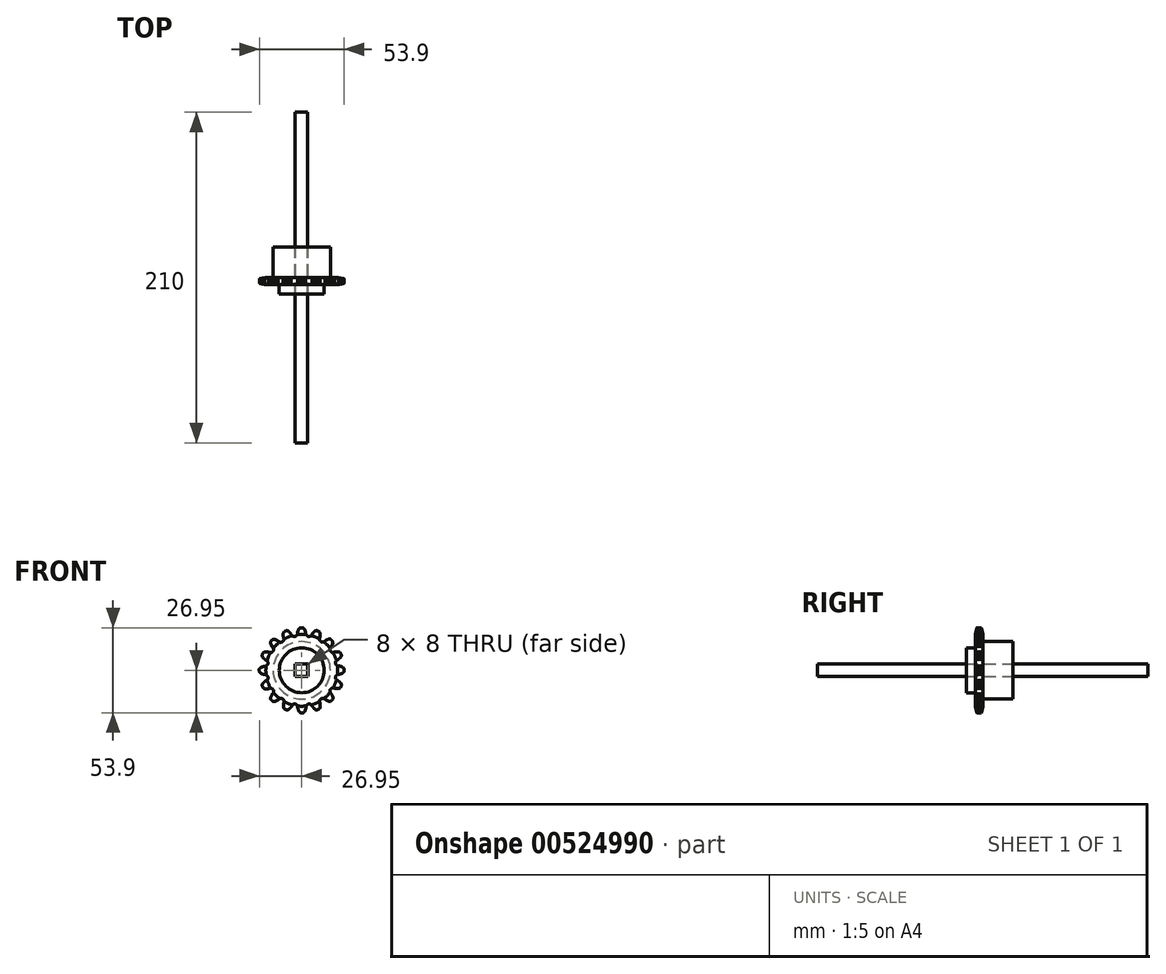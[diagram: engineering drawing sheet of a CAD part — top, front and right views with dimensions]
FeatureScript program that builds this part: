
annotation { "Feature Type Name" : "Feature", "Feature Type Description" : "" }
export const myFeature = defineFeature(function(context is Context, id is Id, definition is map)
    precondition{}
    {
        {
            var Q0;
            Q0=qCreatedBy(makeId("Front.planeOp"),FACE);
            var sketch = newSketch(context, id + "F0", { "sketchPlane" : qUnion([Q0])});
            skCircle(sketch, "E0", {"center": v(0, 0) * mm, "radius": 14.28 * mm});
            skCircle(sketch, "E1", {"center": v(0, 0) * mm, "radius": 26.95 * mm});
            skCircle(sketch, "E2", {"center": v(0, 0) * mm, "radius": 21.9 * mm, "construction": true});
            skArc(sketch, "E3", {"start": v(2.57, 23.85) * mm, "mid": v(4.2, 21.5) * mm, "end": v(6.58, 23.12) * mm});
            skLineSegment(sketch, "E4", {"start": v(2.57, 23.85) * mm, "end": v(1.78, 26.12) * mm});
            skLineSegment(sketch, "E5", {"start": v(1.78, 26.12) * mm, "end": v(0.9, 26.93) * mm});
            skLineSegment(sketch, "E6", {"start": v(6.58, 23.12) * mm, "end": v(8.2, 24.88) * mm});
            skLineSegment(sketch, "E7", {"start": v(8.2, 24.88) * mm, "end": v(9.34, 25.28) * mm});
            skLineSegment(sketch, "E8.1.0", {"start": v(-8.35, 24.81) * mm, "end": v(-9.48, 25.23) * mm});
            skLineSegment(sketch, "E8.1.1", {"start": v(-6.75, 23.02) * mm, "end": v(-8.35, 24.81) * mm});
            skArc(sketch, "E8.1.2", {"start": v(-6.75, 23.02) * mm, "mid": v(-4.34, 21.47) * mm, "end": v(-2.77, 23.88) * mm});
            skLineSegment(sketch, "E8.1.3", {"start": v(-2.77, 23.88) * mm, "end": v(-1.94, 26.13) * mm});
            skLineSegment(sketch, "E8.1.4", {"start": v(-1.94, 26.13) * mm, "end": v(-1.05, 26.93) * mm});
            skLineSegment(sketch, "E8.2.0", {"start": v(-17.21, 19.73) * mm, "end": v(-18.4, 19.68) * mm});
            skLineSegment(sketch, "E8.2.1", {"start": v(-15.05, 18.68) * mm, "end": v(-17.21, 19.73) * mm});
            skArc(sketch, "E8.2.2", {"start": v(-15.05, 18.68) * mm, "mid": v(-12.22, 18.17) * mm, "end": v(-11.7, 21) * mm});
            skLineSegment(sketch, "E8.2.3", {"start": v(-11.7, 21) * mm, "end": v(-11.8, 23.4) * mm});
            skLineSegment(sketch, "E8.2.4", {"start": v(-11.8, 23.4) * mm, "end": v(-11.27, 24.48) * mm});
            skLineSegment(sketch, "E9.2.3.0", {"start": v(-23.45, 11.64) * mm, "end": v(-24.54, 11.14) * mm});
            skLineSegment(sketch, "E9.3.3.0", {"start": v(-21.05, 11.5) * mm, "end": v(-23.45, 11.64) * mm});
            skArc(sketch, "E9.6.3.0", {"start": v(-21.05, 11.5) * mm, "mid": v(-18.24, 12.11) * mm, "end": v(-18.84, 14.93) * mm});
            skLineSegment(sketch, "E9.10.3.0", {"start": v(-18.84, 14.93) * mm, "end": v(-19.85, 17.1) * mm});
            skLineSegment(sketch, "E9.13.3.0", {"start": v(-19.85, 17.1) * mm, "end": v(-19.78, 18.3) * mm});
            skLineSegment(sketch, "E9.2.4.0", {"start": v(-26.12, 1.78) * mm, "end": v(-26.93, 0.9) * mm});
            skLineSegment(sketch, "E9.3.4.0", {"start": v(-23.85, 2.57) * mm, "end": v(-26.12, 1.78) * mm});
            skArc(sketch, "E9.6.4.0", {"start": v(-23.85, 2.57) * mm, "mid": v(-21.5, 4.2) * mm, "end": v(-23.12, 6.58) * mm});
            skLineSegment(sketch, "E9.10.4.0", {"start": v(-23.12, 6.58) * mm, "end": v(-24.88, 8.2) * mm});
            skLineSegment(sketch, "E9.13.4.0", {"start": v(-24.88, 8.2) * mm, "end": v(-25.28, 9.34) * mm});
            skLineSegment(sketch, "E9.2.5.0", {"start": v(-24.81, -8.35) * mm, "end": v(-25.23, -9.48) * mm});
            skLineSegment(sketch, "E9.3.5.0", {"start": v(-23.02, -6.75) * mm, "end": v(-24.81, -8.35) * mm});
            skArc(sketch, "E9.6.5.0", {"start": v(-23.02, -6.75) * mm, "mid": v(-21.47, -4.34) * mm, "end": v(-23.88, -2.77) * mm});
            skLineSegment(sketch, "E9.10.5.0", {"start": v(-23.88, -2.77) * mm, "end": v(-26.13, -1.94) * mm});
            skLineSegment(sketch, "E9.13.5.0", {"start": v(-26.13, -1.94) * mm, "end": v(-26.93, -1.05) * mm});
            skLineSegment(sketch, "E9.2.6.0", {"start": v(-19.73, -17.21) * mm, "end": v(-19.68, -18.4) * mm});
            skLineSegment(sketch, "E9.3.6.0", {"start": v(-18.68, -15.05) * mm, "end": v(-19.73, -17.21) * mm});
            skArc(sketch, "E9.6.6.0", {"start": v(-18.68, -15.05) * mm, "mid": v(-18.17, -12.22) * mm, "end": v(-21, -11.7) * mm});
            skLineSegment(sketch, "E9.10.6.0", {"start": v(-21, -11.7) * mm, "end": v(-23.4, -11.8) * mm});
            skLineSegment(sketch, "E9.13.6.0", {"start": v(-23.4, -11.8) * mm, "end": v(-24.48, -11.27) * mm});
            skLineSegment(sketch, "E9.2.7.0", {"start": v(-11.64, -23.45) * mm, "end": v(-11.14, -24.54) * mm});
            skLineSegment(sketch, "E9.3.7.0", {"start": v(-11.5, -21.05) * mm, "end": v(-11.64, -23.45) * mm});
            skArc(sketch, "E9.6.7.0", {"start": v(-11.5, -21.05) * mm, "mid": v(-12.11, -18.24) * mm, "end": v(-14.93, -18.84) * mm});
            skLineSegment(sketch, "E9.10.7.0", {"start": v(-14.93, -18.84) * mm, "end": v(-17.1, -19.85) * mm});
            skLineSegment(sketch, "E9.13.7.0", {"start": v(-17.1, -19.85) * mm, "end": v(-18.3, -19.78) * mm});
            skLineSegment(sketch, "E9.2.8.0", {"start": v(-1.78, -26.12) * mm, "end": v(-0.9, -26.93) * mm});
            skLineSegment(sketch, "E9.3.8.0", {"start": v(-2.57, -23.85) * mm, "end": v(-1.78, -26.12) * mm});
            skArc(sketch, "E9.6.8.0", {"start": v(-2.57, -23.85) * mm, "mid": v(-4.2, -21.5) * mm, "end": v(-6.58, -23.12) * mm});
            skLineSegment(sketch, "E9.10.8.0", {"start": v(-6.58, -23.12) * mm, "end": v(-8.2, -24.88) * mm});
            skLineSegment(sketch, "E9.13.8.0", {"start": v(-8.2, -24.88) * mm, "end": v(-9.34, -25.28) * mm});
            skLineSegment(sketch, "E9.2.9.0", {"start": v(8.35, -24.81) * mm, "end": v(9.48, -25.23) * mm});
            skLineSegment(sketch, "E9.3.9.0", {"start": v(6.75, -23.02) * mm, "end": v(8.35, -24.81) * mm});
            skArc(sketch, "E9.6.9.0", {"start": v(6.75, -23.02) * mm, "mid": v(4.34, -21.47) * mm, "end": v(2.77, -23.88) * mm});
            skLineSegment(sketch, "E9.10.9.0", {"start": v(2.77, -23.88) * mm, "end": v(1.94, -26.13) * mm});
            skLineSegment(sketch, "E9.13.9.0", {"start": v(1.94, -26.13) * mm, "end": v(1.05, -26.93) * mm});
            skLineSegment(sketch, "E9.2.10.0", {"start": v(17.21, -19.73) * mm, "end": v(18.4, -19.68) * mm});
            skLineSegment(sketch, "E9.3.10.0", {"start": v(15.05, -18.68) * mm, "end": v(17.21, -19.73) * mm});
            skArc(sketch, "E9.6.10.0", {"start": v(15.05, -18.68) * mm, "mid": v(12.22, -18.17) * mm, "end": v(11.7, -21) * mm});
            skLineSegment(sketch, "E9.10.10.0", {"start": v(11.7, -21) * mm, "end": v(11.8, -23.4) * mm});
            skLineSegment(sketch, "E9.13.10.0", {"start": v(11.8, -23.4) * mm, "end": v(11.27, -24.48) * mm});
            skLineSegment(sketch, "E9.2.11.0", {"start": v(23.45, -11.64) * mm, "end": v(24.54, -11.14) * mm});
            skLineSegment(sketch, "E9.3.11.0", {"start": v(21.05, -11.5) * mm, "end": v(23.45, -11.64) * mm});
            skArc(sketch, "E9.6.11.0", {"start": v(21.05, -11.5) * mm, "mid": v(18.24, -12.11) * mm, "end": v(18.84, -14.93) * mm});
            skLineSegment(sketch, "E9.10.11.0", {"start": v(18.84, -14.93) * mm, "end": v(19.85, -17.1) * mm});
            skLineSegment(sketch, "E9.13.11.0", {"start": v(19.85, -17.1) * mm, "end": v(19.78, -18.3) * mm});
            skLineSegment(sketch, "E9.2.12.0", {"start": v(26.12, -1.78) * mm, "end": v(26.93, -0.9) * mm});
            skLineSegment(sketch, "E9.3.12.0", {"start": v(23.85, -2.57) * mm, "end": v(26.12, -1.78) * mm});
            skArc(sketch, "E9.6.12.0", {"start": v(23.85, -2.57) * mm, "mid": v(21.5, -4.2) * mm, "end": v(23.12, -6.58) * mm});
            skLineSegment(sketch, "E9.10.12.0", {"start": v(23.12, -6.58) * mm, "end": v(24.88, -8.2) * mm});
            skLineSegment(sketch, "E9.13.12.0", {"start": v(24.88, -8.2) * mm, "end": v(25.28, -9.34) * mm});
            skLineSegment(sketch, "E9.2.13.0", {"start": v(24.81, 8.35) * mm, "end": v(25.23, 9.48) * mm});
            skLineSegment(sketch, "E9.3.13.0", {"start": v(23.02, 6.75) * mm, "end": v(24.81, 8.35) * mm});
            skArc(sketch, "E9.6.13.0", {"start": v(23.02, 6.75) * mm, "mid": v(21.47, 4.34) * mm, "end": v(23.88, 2.77) * mm});
            skLineSegment(sketch, "E9.10.13.0", {"start": v(23.88, 2.77) * mm, "end": v(26.13, 1.94) * mm});
            skLineSegment(sketch, "E9.13.13.0", {"start": v(26.13, 1.94) * mm, "end": v(26.93, 1.05) * mm});
            skLineSegment(sketch, "E9.2.14.0", {"start": v(19.73, 17.21) * mm, "end": v(19.68, 18.4) * mm});
            skLineSegment(sketch, "E9.3.14.0", {"start": v(18.68, 15.05) * mm, "end": v(19.73, 17.21) * mm});
            skArc(sketch, "E9.6.14.0", {"start": v(18.68, 15.05) * mm, "mid": v(18.17, 12.22) * mm, "end": v(21, 11.7) * mm});
            skLineSegment(sketch, "E9.10.14.0", {"start": v(21, 11.7) * mm, "end": v(23.4, 11.8) * mm});
            skLineSegment(sketch, "E9.13.14.0", {"start": v(23.4, 11.8) * mm, "end": v(24.48, 11.27) * mm});
            skLineSegment(sketch, "E9.2.15.0", {"start": v(11.64, 23.45) * mm, "end": v(11.14, 24.54) * mm});
            skLineSegment(sketch, "E9.3.15.0", {"start": v(11.5, 21.05) * mm, "end": v(11.64, 23.45) * mm});
            skArc(sketch, "E9.6.15.0", {"start": v(11.5, 21.05) * mm, "mid": v(12.11, 18.24) * mm, "end": v(14.93, 18.84) * mm});
            skLineSegment(sketch, "E9.10.15.0", {"start": v(14.93, 18.84) * mm, "end": v(17.1, 19.85) * mm});
            skLineSegment(sketch, "E9.13.15.0", {"start": v(17.1, 19.85) * mm, "end": v(18.3, 19.78) * mm});
            skSolve(sketch);
        }
        {
            var Q0;
            Q0=makeQuery(id+"F0.imprint","IMPRINT",FACE,{"disambiguationData":[TD([[makeQuery(id+"F0.imprint","IMPRINT",EDGE,{"derivedFrom":sQuery(id+"F0.wireOp",EDGE,"E0")}),-1.0]])]});
            extrude(context, id + "F1", {"entities" : qUnion([Q0]), "depth" : 4.5 * mm, "offsetDistance" : 25 * mm});
        }
        {
            var Q0;
            Q0=qCreatedBy(makeId("Right.planeOp"),FACE);
            var sketch = newSketch(context, id + "F2", { "sketchPlane" : qUnion([Q0])});
            skLineSegment(sketch, "E10.bottom", {"start": v(-7.87, 18.82) * mm, "end": v(-5.25, 18.82) * mm});
            skLineSegment(sketch, "E10.top", {"start": v(-7.87, 36.62) * mm, "end": v(3.37, 36.62) * mm});
            skLineSegment(sketch, "E10.left", {"start": v(-7.87, 18.82) * mm, "end": v(-7.87, 36.62) * mm});
            skLineSegment(sketch, "E10.right", {"start": v(3.37, 18.82) * mm, "end": v(3.37, 36.62) * mm});
            skPoint(sketch, "E11", {"position": v(-2.25, 18.82) * mm});
            skLineSegment(sketch, "E12", {"start": v(-5.25, 18.82) * mm, "end": v(-2.25, 34.82) * mm});
            skLineSegment(sketch, "E13", {"start": v(-2.25, 34.82) * mm, "end": v(0.75, 18.82) * mm});
            skLineSegment(sketch, "E14.trimOffspring", {"start": v(0.75, 18.82) * mm, "end": v(3.37, 18.82) * mm});
            skSolve(sketch);
        }
        {
            var Q0;
            Q0=makeQuery(id+"F2.imprint","IMPRINT",FACE,{"disambiguationData":[TD([[makeQuery(id+"F2.imprint","IMPRINT",EDGE,{"derivedFrom":sQuery(id+"F2.wireOp",EDGE,"E10.bottom")}),1.0]])]});
            var Q1;
            Q1=makeQuery(id+"F1.opExtrude","SWEPT_FACE",FACE,{"disambiguationData":[OSD([sQuery(id+"F0.wireOp",EDGE,"E0")])]});
            revolve(context, id + "F3", {"operationType" : NewBodyOperationType.REMOVE, "entities" : qUnion([Q0]), "axis" : qUnion([Q1]), "revolveType" : RevolveType.FULL, "oppositeDirection" : true});
        }
        {
            var Q0;
            Q0=qCreatedBy(makeId("Front.planeOp"),FACE);
            var sketch = newSketch(context, id + "F4", { "sketchPlane" : qUnion([Q0])});
            skCircle(sketch, "E15", {"center": v(0, 0) * mm, "radius": 14.28 * mm});
            skCircle(sketch, "E16", {"center": v(0, 0) * mm, "radius": 18.2 * mm});
            skSolve(sketch);
        }
        {
            var Q0;
            Q0 = qSketchRegion(id + "F4", true);
            var Q1;
            Q1=makeQuery(id+"F4.imprint","IMPRINT",FACE,{"disambiguationData":[TD([[makeQuery(id+"F4.imprint","IMPRINT",EDGE,{"derivedFrom":sQuery(id+"F4.wireOp",EDGE,"E15")}),-1.0]])]});
            var Q2;
            Q2=makeQuery(id+"F4.imprint","IMPRINT",FACE,{"disambiguationData":[TD([[makeQuery(id+"F4.imprint","IMPRINT",EDGE,{"derivedFrom":sQuery(id+"F4.wireOp",EDGE,"E15")}),1.0]])]});
            extrude(context, id + "F5", {"entities" : qUnion([Q0, Q1, Q2]), "operationType" : NewBodyOperationType.ADD, "oppositeDirection" : true, "depth" : 19.3 * mm, "offsetDistance" : 25 * mm});
        }
        {
            var Q0;
            Q0=makeQuery(id+"F4.imprint","IMPRINT",FACE,{"disambiguationData":[TD([[makeQuery(id+"F4.imprint","IMPRINT",EDGE,{"derivedFrom":sQuery(id+"F4.wireOp",EDGE,"E15")}),1.0]])]});
            extrude(context, id + "F6", {"entities" : qUnion([Q0]), "operationType" : NewBodyOperationType.ADD, "depth" : 10.5 * mm, "offsetDistance" : 25 * mm});
        }
        {
            var Q0;
            Q0=makeQuery(id+"F5.opExtrude","CAP_FACE",FACE,{"disambiguationData":[OSD([sQuery(id+"F4.wireOp",EDGE,"E16")])],"isStart":false});
            var sketch = newSketch(context, id + "F7", { "sketchPlane" : qUnion([Q0])});
            skCircle(sketch, "E17.cCircle", {"center": v(0, 0) * mm, "radius": 5.66 * mm, "construction": true});
            skLineSegment(sketch, "E17.0", {"start": v(-4, 4) * mm, "end": v(4, 4) * mm});
            skLineSegment(sketch, "E17.1", {"start": v(4, 4) * mm, "end": v(4, -4) * mm});
            skLineSegment(sketch, "E17.2", {"start": v(4, -4) * mm, "end": v(-4, -4) * mm});
            skLineSegment(sketch, "E17.3", {"start": v(-4, -4) * mm, "end": v(-4, 4) * mm});
            skSolve(sketch);
        }
        {
            var Q0;
            Q0 = qSketchRegion(id + "F7", true);
            var Q1;
            Q1=makeQuery(id+"F7.imprint","IMPRINT",FACE,{"disambiguationData":[TD([[makeQuery(id+"F7.imprint","IMPRINT",EDGE,{"derivedFrom":sQuery(id+"F7.wireOp",EDGE,"E17.0")}),-1.0]])]});
            extrude(context, id + "F8", {"entities" : qUnion([Q0, Q1]), "operationType" : NewBodyOperationType.REMOVE, "endBound" : BoundingType.THROUGH_ALL, "oppositeDirection" : true, "depth" : 25 * mm, "offsetDistance" : 25 * mm});
        }
        {
            var Q0;
            Q0=qCreatedBy(makeId("Front.planeOp"),FACE);
            var sketch = newSketch(context, id + "F9", { "sketchPlane" : qUnion([Q0])});
            skLineSegment(sketch, "E18.bottom", {"start": v(-4.11, 3.95) * mm, "end": v(3.79, 3.95) * mm});
            skLineSegment(sketch, "E18.top", {"start": v(-4.11, -3.95) * mm, "end": v(3.79, -3.95) * mm});
            skLineSegment(sketch, "E18.left", {"start": v(-4.11, 3.95) * mm, "end": v(-4.11, -3.95) * mm});
            skLineSegment(sketch, "E18.right", {"start": v(3.79, 3.95) * mm, "end": v(3.79, -3.95) * mm});
            skSolve(sketch);
        }
        {
            var Q0;
            Q0 = qSketchRegion(id + "F9", true);
            var Q1;
            Q1=makeQuery(id+"F9.imprint","IMPRINT",FACE,{"disambiguationData":[TD([[makeQuery(id+"F9.imprint","IMPRINT",EDGE,{"derivedFrom":sQuery(id+"F9.wireOp",EDGE,"E18.bottom")}),-1.0]])]});
            extrude(context, id + "F10", {"entities" : qUnion([Q0, Q1]), "depth" : 210 * mm, "offsetDistance" : 25 * mm, "symmetric" : true});
        }
    });
